# Revit family: IS_ConnectAir_E2288_BIM_DE
name_source: partatom
category: Generic Models
units: mm (PartAtom-declared; Revit-internal decimal feet)

## family parameters
Always vertical = No
Can host rebar = No
Cut with Voids When Loaded = No
OmniClass Number = 23.31.19.00
Part Type = Normal
Room Calculation Point = No
Round Connector Dimension = Use Diameter
Shared = No
Work Plane-Based = No

## types (2) — shared parameters
BIMobject category = Plumbing Fitures
Brand url = http://www.idealstandard.de
Description = Connect Air wall hung WC Bowl with hidden fixation. Boxed
Edition number = 1
GTIN code = https://5017830553595
IFC Classification = Sanitary Terminal
Installation instructions = https://www.idealstandard.de
Manufacturer = Ideal Standard
Manufacturer name = Ideal Standard
Material main = Ceramics
NBS Reference Code = 45-35-70/384
NBS Reference Description = Wc Pans
NominalDepth = 543 mm
NominalHeight = 347 mm
NominalWidth = 362 mm
OmniClass Code = 23-31 19 00
OmniClass Description = Toilets
Product Guid = 85990abe-dd62-462d-a87d-747c03281acc
Product certification = https://www.idealstandard.de
Product data url = https://bimobject.com
Product name = Connect Air WC Bowl
Product url = https://www.idealstandard.de
QR code = http://bimobject.com
Size = 543 x 363 x 347 mm
Technical description = https://www.idealstandard.de
UNSPSC Code = 301815
URL = https://www.idealstandard.de
Uniclass 1.4 Code = L7216
Uniclass 1.4 Description = Toilets
Uniclass 2.0 Code = PR-35-93-94
Uniclass 2.0 Description = Wc Pans
Uniclass 2015 Code = Pr_40_20_93_94
Uniclass 2015 Name = WC pans
Youtube clip = https://www.youtube.com
zero-valued in all types: Cost

## per-type parameters (varying)
| type | BIMobject main category | Model | Product SKU | Product family | Product group |
| E228801 - CONNECT AIR WHG BWL WHT RL+ HF BXD | Toilet | E228801 | E228801 | Sanitary | WC Pan |
| E2288V3 - CONNECT AIR WHG BWL RL+ HF SILKBL BXD | WC Pan | E2288V3 | E2288V3 | Connect Air | WC Pans |

## geometry (parser evidence)
native form markers: Sweep x4
no freeform markers — native parametric forms only
